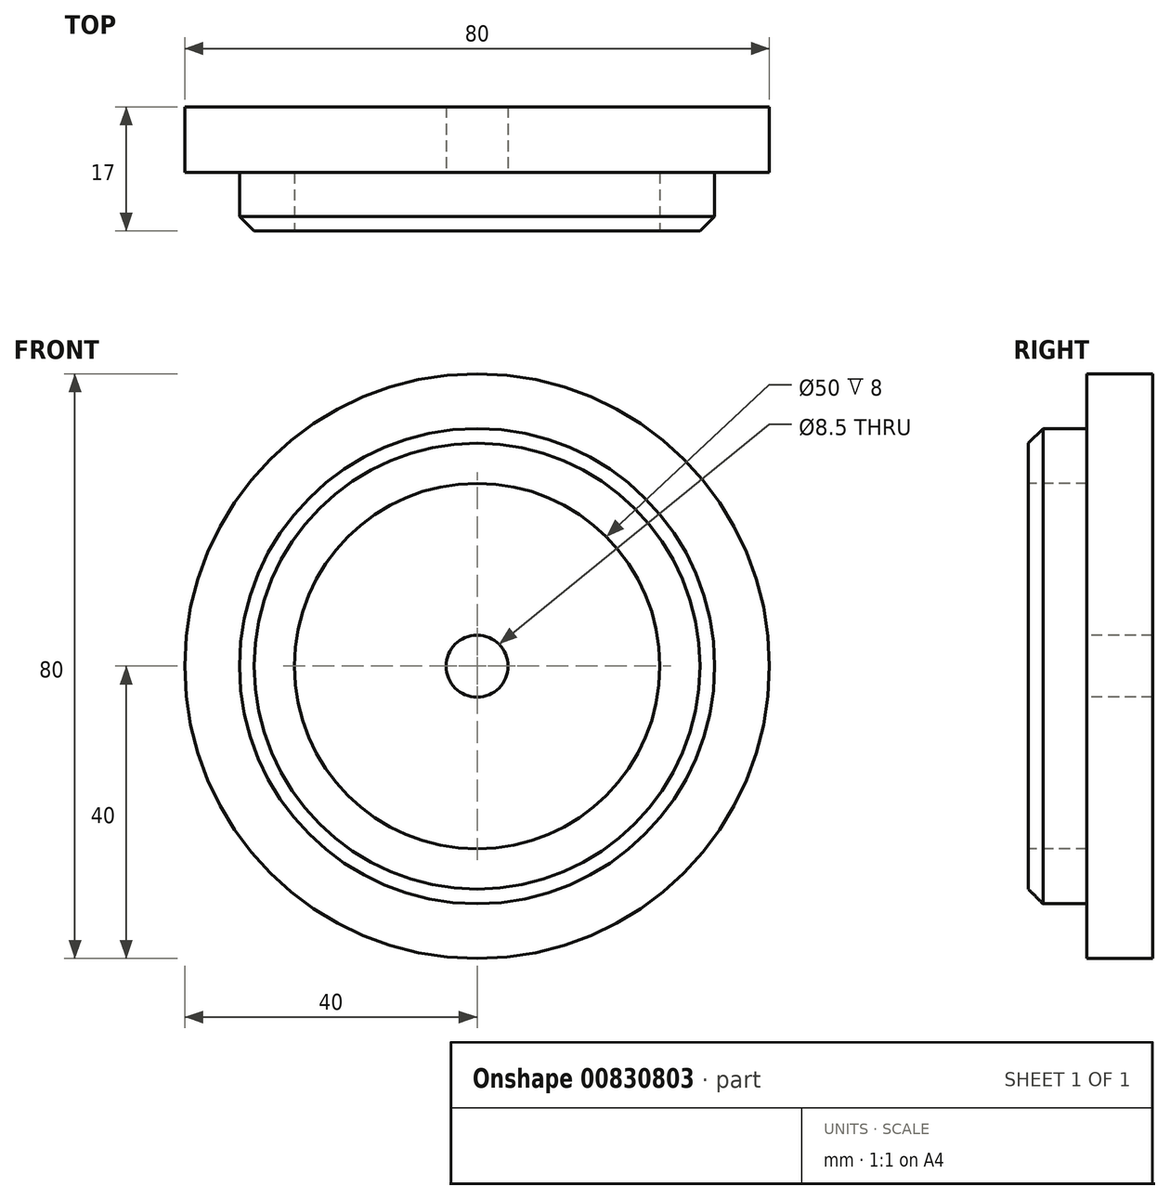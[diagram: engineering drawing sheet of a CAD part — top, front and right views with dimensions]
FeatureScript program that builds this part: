
annotation { "Feature Type Name" : "Feature", "Feature Type Description" : "" }
export const myFeature = defineFeature(function(context is Context, id is Id, definition is map)
    precondition{}
    {
        {
            var Q0;
            Q0=qCreatedBy(makeId("Front.planeOp"),FACE);
            var sketch = newSketch(context, id + "F0", { "sketchPlane" : qUnion([Q0])});
            skCircle(sketch, "E0", {"center": v(0, 0) * mm, "radius": 40 * mm});
            skSolve(sketch);
        }
        {
            var Q0;
            Q0=makeQuery(id+"F0.imprint","IMPRINT",FACE,{"disambiguationData":[TD([[makeQuery(id+"F0.imprint","IMPRINT",EDGE,{"derivedFrom":sQuery(id+"F0.wireOp",EDGE,"E0")}),1.0]])]});
            extrude(context, id + "F1", {"entities" : qUnion([Q0]), "depth" : 9 * mm, "offsetDistance" : 25 * mm});
        }
        {
            var Q0;
            Q0=makeQuery(id+"F1.opExtrude","CAP_FACE",FACE,{"disambiguationData":[OSD([sQuery(id+"F0.wireOp",EDGE,"E0")])],"isStart":false});
            var sketch = newSketch(context, id + "F2", { "sketchPlane" : qUnion([Q0])});
            skCircle(sketch, "E1", {"center": v(0, 0) * mm, "radius": 32.5 * mm});
            skSolve(sketch);
        }
        {
            var Q0;
            Q0=makeQuery(id+"F2.imprint","IMPRINT",FACE,{"disambiguationData":[TD([[makeQuery(id+"F2.imprint","IMPRINT",EDGE,{"derivedFrom":sQuery(id+"F2.wireOp",EDGE,"E1")}),1.0]])]});
            extrude(context, id + "F3", {"entities" : qUnion([Q0]), "operationType" : NewBodyOperationType.ADD, "depth" : 8 * mm, "offsetDistance" : 25 * mm});
        }
        {
            var Q0;
            Q0=makeQuery(id+"F3.opExtrude","CAP_FACE",FACE,{"disambiguationData":[OSD([sQuery(id+"F2.wireOp",EDGE,"E1")])],"isStart":false});
            var sketch = newSketch(context, id + "F4", { "sketchPlane" : qUnion([Q0])});
            skPoint(sketch, "E2", {"position": v(0, 0) * mm});
            skCircle(sketch, "E3", {"center": v(0, 0) * mm, "radius": 25 * mm});
            skSolve(sketch);
        }
        {
            var Q0;
            Q0=makeQuery(id+"F4.imprint","IMPRINT",FACE,{"disambiguationData":[TD([[makeQuery(id+"F4.imprint","IMPRINT",EDGE,{"derivedFrom":sQuery(id+"F4.wireOp",EDGE,"E3")}),1.0]])]});
            extrude(context, id + "F5", {"entities" : qUnion([Q0]), "operationType" : NewBodyOperationType.REMOVE, "oppositeDirection" : true, "depth" : 8 * mm, "offsetDistance" : 25 * mm});
        }
        {
            var Q0;
            Q0=makeQuery(id+"F5.boolean.opBoolean","COPY",FACE,{"derivedFrom":makeQuery(id+"F5.opExtrude","CAP_FACE",FACE,{"disambiguationData":[OSD([sQuery(id+"F4.wireOp",EDGE,"E3")])],"isStart":false})});
            var sketch = newSketch(context, id + "F6", { "sketchPlane" : qUnion([Q0])});
            skPoint(sketch, "E4", {"position": v(0, 0) * mm});
            skCircle(sketch, "E5", {"center": v(0, 0) * mm, "radius": 4.25 * mm});
            skSolve(sketch);
        }
        {
            var Q0;
            Q0=makeQuery(id+"F6.imprint","IMPRINT",FACE,{"disambiguationData":[TD([[makeQuery(id+"F6.imprint","IMPRINT",EDGE,{"derivedFrom":sQuery(id+"F6.wireOp",EDGE,"E5")}),1.0]])]});
            extrude(context, id + "F7", {"entities" : qUnion([Q0]), "operationType" : NewBodyOperationType.REMOVE, "oppositeDirection" : true, "depth" : 25 * mm, "offsetDistance" : 25 * mm});
        }
        {
            var Q0;
            Q0=makeQuery(id+"F3.opExtrude","CAP_EDGE",EDGE,{"disambiguationData":[OSD([sQuery(id+"F2.wireOp",EDGE,"E1")])],"isStart":false});
            chamfer(context, id + "F8", {"entities" : qUnion([Q0]), "width" : 2 * mm, "tangentPropagation" : true});
        }
    });
